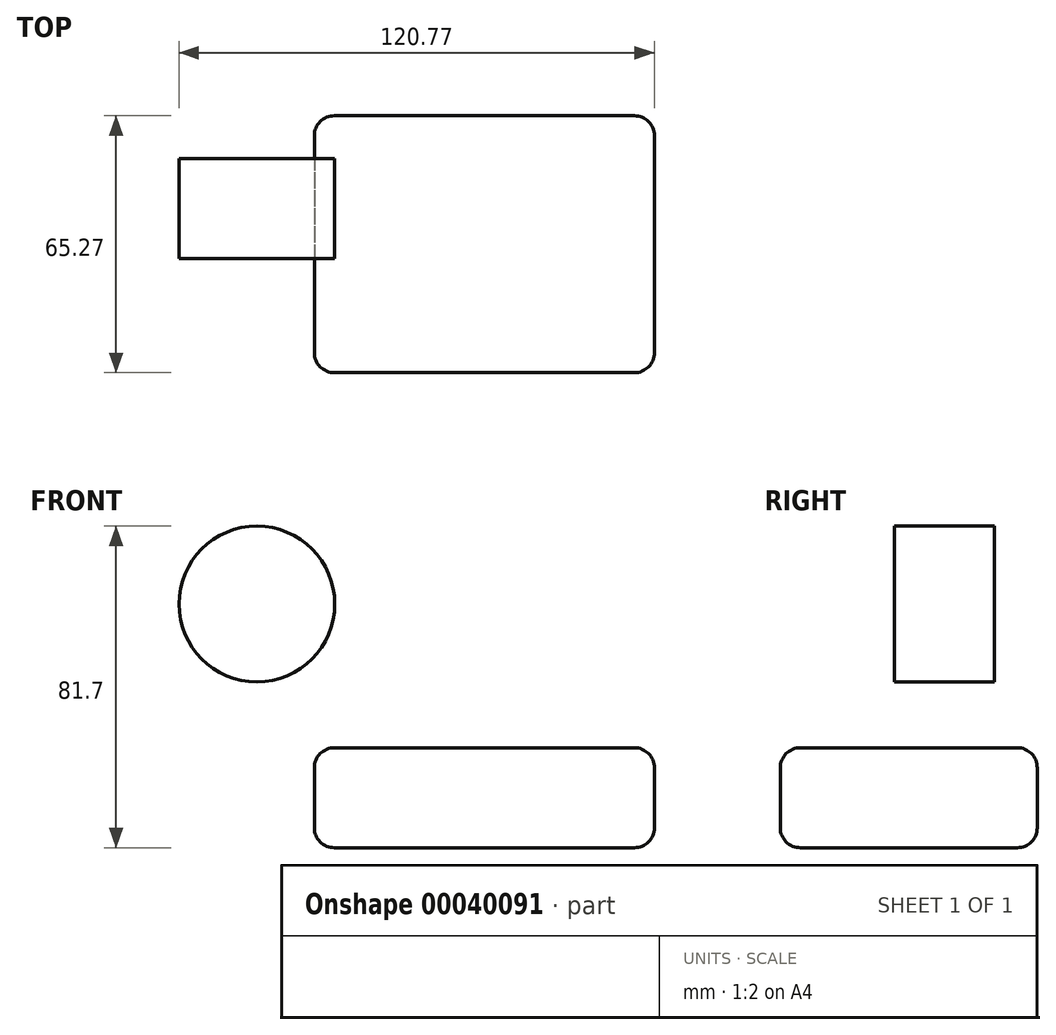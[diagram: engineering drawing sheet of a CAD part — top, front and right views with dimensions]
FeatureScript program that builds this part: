
annotation { "Feature Type Name" : "Feature", "Feature Type Description" : "" }
export const myFeature = defineFeature(function(context is Context, id is Id, definition is map)
    precondition{}
    {
        {
            var Q0;
            Q0=qCreatedBy(makeId("Top.planeOp"),FACE);
            var sketch = newSketch(context, id + "F0", { "sketchPlane" : qUnion([Q0])});
            skLineSegment(sketch, "E0.bottom", {"start": v(-44.3, 36.27) * mm, "end": v(42.08, 36.27) * mm});
            skLineSegment(sketch, "E0.top", {"start": v(-44.3, -29) * mm, "end": v(42.08, -29) * mm});
            skLineSegment(sketch, "E0.left", {"start": v(-44.3, 36.27) * mm, "end": v(-44.3, -29) * mm});
            skLineSegment(sketch, "E0.right", {"start": v(42.08, 36.27) * mm, "end": v(42.08, -29) * mm});
            skSolve(sketch);
        }
        {
            var Q0;
            Q0 = qSketchRegion(id + "F0", true);
            var Q1;
            Q1=makeQuery(id+"F0.imprint","IMPRINT",FACE,{"disambiguationData":[TD([[makeQuery(id+"F0.imprint","IMPRINT",EDGE,{"derivedFrom":sQuery(id+"F0.wireOp",EDGE,"E0.bottom")}),-1.0]])]});
            extrude(context, id + "F1", {"entities" : qUnion([Q0, Q1]), "depth" : 25.4 * mm});
        }
        {
            var Q0;
            Q0=makeQuery(id+"F1.opExtrude","SWEPT_FACE",FACE,{"disambiguationData":[OSD([sQuery(id+"F0.wireOp",EDGE,"E0.top")])]});
            var Q1;
            Q1=makeQuery(id+"F1.opExtrude","SWEPT_FACE",FACE,{"disambiguationData":[OSD([sQuery(id+"F0.wireOp",EDGE,"E0.right")])]});
            var Q2;
            Q2=makeQuery(id+"F1.opExtrude","SWEPT_FACE",FACE,{"disambiguationData":[OSD([sQuery(id+"F0.wireOp",EDGE,"E0.left")])]});
            var Q3;
            Q3=makeQuery(id+"F1.opExtrude","SWEPT_FACE",FACE,{"disambiguationData":[OSD([sQuery(id+"F0.wireOp",EDGE,"E0.bottom")])]});
            fillet(context, id + "F2", {"entities" : qUnion([Q0, Q1, Q2, Q3]), "radius" : 5.08 * mm, "allowEdgeOverflow" : false});
        }
        {
            var Q0;
            Q0=qCreatedBy(makeId("Front.planeOp"),FACE);
            var sketch = newSketch(context, id + "F3", { "sketchPlane" : qUnion([Q0])});
            skCircle(sketch, "E1", {"center": v(-58.9, 61.91) * mm, "radius": 19.8 * mm});
            skSolve(sketch);
        }
        {
            var Q0;
            Q0=makeQuery(id+"F3.imprint","IMPRINT",FACE,{"disambiguationData":[TD([[makeQuery(id+"F3.imprint","IMPRINT",EDGE,{"derivedFrom":sQuery(id+"F3.wireOp",EDGE,"E1")}),1.0]])]});
            extrude(context, id + "F4", {"entities" : qUnion([Q0]), "oppositeDirection" : true, "depth" : 25.4 * mm});
        }
    });
